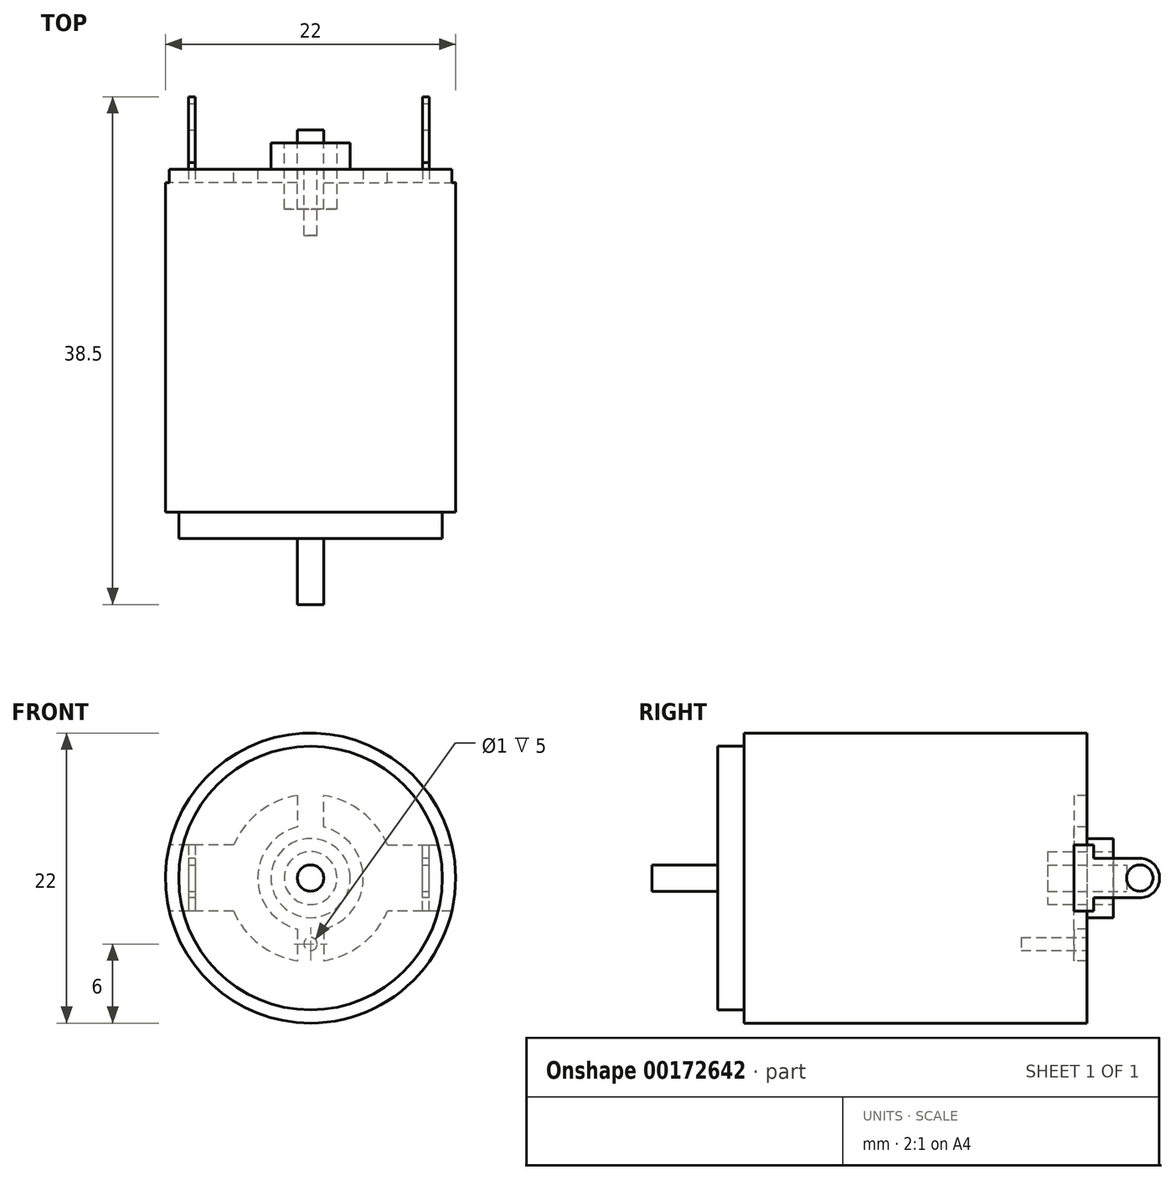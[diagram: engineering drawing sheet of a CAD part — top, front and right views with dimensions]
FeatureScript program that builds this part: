
annotation { "Feature Type Name" : "Feature", "Feature Type Description" : "" }
export const myFeature = defineFeature(function(context is Context, id is Id, definition is map)
    precondition{}
    {
        {
            var Q0;
            Q0=qCreatedBy(makeId("Front.planeOp"),FACE);
            var sketch = newSketch(context, id + "F0", { "sketchPlane" : qUnion([Q0])});
            skCircle(sketch, "E0", {"center": v(0, 0) * mm, "radius": 11 * mm});
            skSolve(sketch);
        }
        {
            var Q0;
            Q0 = qSketchRegion(id + "F0", true);
            extrude(context, id + "F1", {"entities" : qUnion([Q0]), "depth" : 26 * mm});
        }
        {
            var Q0;
            Q0=makeQuery(id+"F1.opExtrude","CAP_FACE",FACE,{"disambiguationData":[OSD([sQuery(id+"F0.wireOp",EDGE,"E0")])],"isStart":false});
            var sketch = newSketch(context, id + "F2", { "sketchPlane" : qUnion([Q0])});
            skCircle(sketch, "E1", {"center": v(0, 0) * mm, "radius": 10 * mm});
            skSolve(sketch);
        }
        {
            var Q0;
            Q0 = qSketchRegion(id + "F2", true);
            extrude(context, id + "F3", {"entities" : qUnion([Q0]), "operationType" : NewBodyOperationType.ADD, "depth" : 2 * mm});
        }
        {
            var Q0;
            Q0=makeQuery(id+"F3.opExtrude","CAP_FACE",FACE,{"disambiguationData":[OSD([sQuery(id+"F2.wireOp",EDGE,"E1")])],"isStart":false});
            var sketch = newSketch(context, id + "F4", { "sketchPlane" : qUnion([Q0])});
            skCircle(sketch, "E2", {"center": v(0, 0) * mm, "radius": 1 * mm});
            skSolve(sketch);
        }
        {
            var Q0;
            Q0 = qSketchRegion(id + "F4", true);
            extrude(context, id + "F5", {"entities" : qUnion([Q0]), "operationType" : NewBodyOperationType.ADD, "depth" : 5 * mm});
        }
        {
            var Q0;
            Q0=makeQuery(id+"F1.opExtrude","CAP_FACE",FACE,{"disambiguationData":[OSD([sQuery(id+"F0.wireOp",EDGE,"E0")])],"isStart":true});
            var sketch = newSketch(context, id + "F6", { "sketchPlane" : qUnion([Q0])});
            skArc(sketch, "E3", {"start": v(-5.84, -2.5) * mm, "mid": v(0, -6.35) * mm, "end": v(5.84, -2.5) * mm});
            skLineSegment(sketch, "E4", {"start": v(-5.84, 2.5) * mm, "end": v(-10.71, 2.5) * mm});
            skLineSegment(sketch, "E5", {"start": v(5.84, 2.5) * mm, "end": v(10.71, 2.5) * mm});
            skLineSegment(sketch, "E6", {"start": v(-10.71, -2.5) * mm, "end": v(-5.84, -2.5) * mm});
            skPoint(sketch, "E7", {"position": v(-5.84, 2.5) * mm});
            skPoint(sketch, "E8", {"position": v(-5.84, -2.5) * mm});
            skPoint(sketch, "E9", {"position": v(5.84, -2.5) * mm});
            skPoint(sketch, "E10", {"position": v(5.84, 2.5) * mm});
            skArc(sketch, "E11.trimOffspring", {"start": v(5.84, 2.5) * mm, "mid": v(0, 6.35) * mm, "end": v(-5.84, 2.5) * mm});
            skLineSegment(sketch, "E12.trimOffspring", {"start": v(5.84, -2.5) * mm, "end": v(10.71, -2.5) * mm});
            skSolve(sketch);
        }
        {
            var Q0;
            Q0=makeQuery(id+"F6.imprint","IMPRINT",FACE,{"disambiguationData":[TD([[makeQuery(id+"F6.imprint","IMPRINT",EDGE,{"derivedFrom":sQuery(id+"F6.wireOp",EDGE,"E3")}),1.0]])]});
            extrude(context, id + "F7", {"entities" : qUnion([Q0]), "operationType" : NewBodyOperationType.REMOVE, "oppositeDirection" : true, "depth" : 1 * mm});
        }
        {
            var Q0;
            Q0=makeQuery(id+"F7.boolean.opBoolean","COPY",FACE,{"derivedFrom":makeQuery(id+"F7.opExtrude","CAP_FACE",FACE,{"disambiguationData":[OSD([sQuery(id+"F0.wireOp",EDGE,"E0"),sQuery(id+"F6.wireOp",EDGE,"E3"),sQuery(id+"F6.wireOp",EDGE,"E4"),sQuery(id+"F6.wireOp",EDGE,"E5"),sQuery(id+"F6.wireOp",EDGE,"E6"),sQuery(id+"F6.wireOp",EDGE,"E11.trimOffspring"),sQuery(id+"F6.wireOp",EDGE,"E12.trimOffspring")])],"isStart":false})});
            var sketch = newSketch(context, id + "F8", { "sketchPlane" : qUnion([Q0])});
            skArc(sketch, "E13", {"start": v(-1, 3.87) * mm, "mid": v(-4, 0) * mm, "end": v(-1, -3.87) * mm});
            skLineSegment(sketch, "E14", {"start": v(-1, 3.87) * mm, "end": v(-1, 6.27) * mm});
            skLineSegment(sketch, "E15", {"start": v(-1, 6.27) * mm, "end": v(-1, 3.87) * mm});
            skLineSegment(sketch, "E16", {"start": v(1, 6.27) * mm, "end": v(1, 3.87) * mm});
            skArc(sketch, "E17.trimOffspring", {"start": v(1, -3.87) * mm, "mid": v(4, 0) * mm, "end": v(1, 3.87) * mm});
            skLineSegment(sketch, "E18.trimOffspring", {"start": v(-1, -3.87) * mm, "end": v(-1, -6.27) * mm});
            skLineSegment(sketch, "E19.trimOffspring", {"start": v(1, -3.87) * mm, "end": v(1, -6.27) * mm});
            skSolve(sketch);
        }
        {
            var Q0;
            Q0=makeQuery(id+"F8.imprint","IMPRINT",FACE,{"disambiguationData":[TD([[makeQuery(id+"F8.imprint","IMPRINT",EDGE,{"derivedFrom":sQuery(id+"F8.wireOp",EDGE,"E13")}),1.0]])]});
            extrude(context, id + "F9", {"entities" : qUnion([Q0]), "operationType" : NewBodyOperationType.ADD, "depth" : 1 * mm});
        }
        {
            var Q0;
            {var subQ0=sQuery(id+"F6.wireOp",EDGE,"E11.trimOffspring");var subQ1=sQuery(id+"F6.wireOp",EDGE,"E3");var subQ2=sQuery(id+"F0.wireOp",EDGE,"E0");var subQ4=makeQuery(id+"F1.opExtrude","CAP_FACE",FACE,{"disambiguationData":[OSD([subQ2])],"isStart":true});Q0=makeQuery(id+"F9.boolean.opBoolean","MERGE",FACE,{"derivedFrom":[makeQuery(id+"F7.boolean.opBoolean","SPLIT",FACE,{"disambiguationData":[TD([makeQuery(id+"F7.opExtrude","SWEPT_FACE",FACE,{"disambiguationData":[OSD([subQ1])]})])],"derivedFrom":subQ4}),makeQuery(id+"F7.boolean.opBoolean","SPLIT",FACE,{"disambiguationData":[TD([makeQuery(id+"F7.opExtrude","SWEPT_FACE",FACE,{"disambiguationData":[OSD([sQuery(id+"F6.wireOp",EDGE,"E4")])]})])],"derivedFrom":subQ4}),makeQuery(id+"F9.opExtrude","CAP_FACE",FACE,{"disambiguationData":[OSD([subQ1,subQ0,sQuery(id+"F8.wireOp",EDGE,"E13"),sQuery(id+"F8.wireOp",EDGE,"E15"),sQuery(id+"F8.wireOp",EDGE,"E16"),sQuery(id+"F8.wireOp",EDGE,"E17.trimOffspring"),sQuery(id+"F8.wireOp",EDGE,"E18.trimOffspring"),sQuery(id+"F8.wireOp",EDGE,"E19.trimOffspring")])],"isStart":false})]});}
            var sketch = newSketch(context, id + "F10", { "sketchPlane" : qUnion([Q0])});
            skCircle(sketch, "E20", {"center": v(0, 0) * mm, "radius": 3 * mm});
            skSolve(sketch);
        }
        {
            var Q0;
            Q0 = qSketchRegion(id + "F10", true);
            extrude(context, id + "F11", {"entities" : qUnion([Q0]), "operationType" : NewBodyOperationType.ADD, "depth" : 2 * mm});
        }
        {
            var Q0;
            Q0=makeQuery(id+"F11.opExtrude","CAP_FACE",FACE,{"disambiguationData":[OSD([sQuery(id+"F10.wireOp",EDGE,"E20")])],"isStart":false});
            var sketch = newSketch(context, id + "F12", { "sketchPlane" : qUnion([Q0])});
            skCircle(sketch, "E21", {"center": v(0, 0) * mm, "radius": 2 * mm});
            skCircle(sketch, "E22", {"center": v(0, 0) * mm, "radius": 1 * mm});
            skSolve(sketch);
        }
        {
            var Q0;
            Q0=makeQuery(id+"F12.imprint","IMPRINT",FACE,{"disambiguationData":[TD([[makeQuery(id+"F12.imprint","IMPRINT",EDGE,{"derivedFrom":sQuery(id+"F12.wireOp",EDGE,"E21")}),1.0]])]});
            extrude(context, id + "F13", {"entities" : qUnion([Q0]), "operationType" : NewBodyOperationType.REMOVE, "oppositeDirection" : true, "depth" : 5 * mm});
        }
        {
            var Q0;
            Q0=makeQuery(id+"F13.boolean.opBoolean","SPLIT",FACE,{"disambiguationData":[TD([makeQuery(id+"F13.opExtrude","SWEPT_FACE",FACE,{"disambiguationData":[OSD([sQuery(id+"F12.wireOp",EDGE,"E22")])]})])],"derivedFrom":makeQuery(id+"F11.opExtrude","CAP_FACE",FACE,{"disambiguationData":[OSD([sQuery(id+"F10.wireOp",EDGE,"E20")])],"isStart":false})});
            extrude(context, id + "F14", {"entities" : qUnion([Q0]), "operationType" : NewBodyOperationType.ADD, "depth" : 1 * mm});
        }
        {
            var Q0;
            {var subQ0=sQuery(id+"F6.wireOp",EDGE,"E11.trimOffspring");var subQ1=sQuery(id+"F6.wireOp",EDGE,"E3");var subQ2=sQuery(id+"F0.wireOp",EDGE,"E0");var subQ4=makeQuery(id+"F1.opExtrude","CAP_FACE",FACE,{"disambiguationData":[OSD([subQ2])],"isStart":true});Q0=makeQuery(id+"F9.boolean.opBoolean","MERGE",FACE,{"derivedFrom":[makeQuery(id+"F7.boolean.opBoolean","SPLIT",FACE,{"disambiguationData":[TD([makeQuery(id+"F7.opExtrude","SWEPT_FACE",FACE,{"disambiguationData":[OSD([subQ1])]})])],"derivedFrom":subQ4}),makeQuery(id+"F7.boolean.opBoolean","SPLIT",FACE,{"disambiguationData":[TD([makeQuery(id+"F7.opExtrude","SWEPT_FACE",FACE,{"disambiguationData":[OSD([sQuery(id+"F6.wireOp",EDGE,"E4")])]})])],"derivedFrom":subQ4}),makeQuery(id+"F9.opExtrude","CAP_FACE",FACE,{"disambiguationData":[OSD([subQ1,subQ0,sQuery(id+"F8.wireOp",EDGE,"E13"),sQuery(id+"F8.wireOp",EDGE,"E15"),sQuery(id+"F8.wireOp",EDGE,"E16"),sQuery(id+"F8.wireOp",EDGE,"E17.trimOffspring"),sQuery(id+"F8.wireOp",EDGE,"E18.trimOffspring"),sQuery(id+"F8.wireOp",EDGE,"E19.trimOffspring")])],"isStart":false})]});}
            var sketch = newSketch(context, id + "F15", { "sketchPlane" : qUnion([Q0])});
            skPoint(sketch, "E23", {"position": v(0, -5) * mm});
            skCircle(sketch, "E24", {"center": v(0, -5) * mm, "radius": 0.5 * mm});
            skSolve(sketch);
        }
        {
            var Q0;
            Q0=makeQuery(id+"F15.imprint","IMPRINT",FACE,{"disambiguationData":[TD([[makeQuery(id+"F15.imprint","IMPRINT",EDGE,{"derivedFrom":sQuery(id+"F15.wireOp",EDGE,"E24")}),1.0]])]});
            var Q1;
            Q1=sQuery(id+"F15.wireOp",EDGE,"E24");
            extrude(context, id + "F16", {"entities" : qUnion([Q0]), "operationType" : NewBodyOperationType.REMOVE, "surfaceEntities" : qUnion([Q1]), "oppositeDirection" : true, "depth" : 5 * mm});
        }
        {
            var Q0;
            {var subQ0=sQuery(id+"F6.wireOp",EDGE,"E6");var subQ1=sQuery(id+"F6.wireOp",EDGE,"E4");var subQ2=sQuery(id+"F6.wireOp",EDGE,"E3");var subQ3=sQuery(id+"F0.wireOp",EDGE,"E0");var subQ4=sQuery(id+"F6.wireOp",EDGE,"E11.trimOffspring");Q0=makeQuery(id+"F9.boolean.opBoolean","SPLIT",FACE,{"disambiguationData":[TD([makeQuery(id+"F7.boolean.opBoolean","COPY",FACE,{"derivedFrom":makeQuery(id+"F7.opExtrude","SWEPT_FACE",FACE,{"disambiguationData":[OSD([subQ1])]})})])],"derivedFrom":makeQuery(id+"F7.boolean.opBoolean","COPY",FACE,{"derivedFrom":makeQuery(id+"F7.opExtrude","CAP_FACE",FACE,{"disambiguationData":[OSD([subQ3,subQ2,subQ1,sQuery(id+"F6.wireOp",EDGE,"E5"),subQ0,subQ4,sQuery(id+"F6.wireOp",EDGE,"E12.trimOffspring")])],"isStart":false})})});}
            var sketch = newSketch(context, id + "F17", { "sketchPlane" : qUnion([Q0])});
            skPoint(sketch, "E25", {"position": v(-11, 0) * mm});
            skPoint(sketch, "E26", {"position": v(-9, 0) * mm});
            skLineSegment(sketch, "E27.bottom", {"start": v(-9, -2.5) * mm, "end": v(-8.5, -2.5) * mm});
            skLineSegment(sketch, "E27.top", {"start": v(-9, 2.5) * mm, "end": v(-8.5, 2.5) * mm});
            skLineSegment(sketch, "E27.left", {"start": v(-9, -2.5) * mm, "end": v(-9, 2.5) * mm});
            skLineSegment(sketch, "E27.right", {"start": v(-8.5, -2.5) * mm, "end": v(-8.5, 2.5) * mm});
            skSolve(sketch);
        }
        {
            var Q0;
            Q0 = qSketchRegion(id + "F17", true);
            extrude(context, id + "F18", {"entities" : qUnion([Q0]), "operationType" : NewBodyOperationType.ADD, "depth" : 1.5 * mm});
        }
        {
            var Q0;
            Q0=makeQuery(id+"F18.opExtrude","CAP_FACE",FACE,{"disambiguationData":[OSD([sQuery(id+"F17.wireOp",EDGE,"E27.bottom"),sQuery(id+"F17.wireOp",EDGE,"E27.top"),sQuery(id+"F17.wireOp",EDGE,"E27.left"),sQuery(id+"F17.wireOp",EDGE,"E27.right")])],"isStart":false});
            var sketch = newSketch(context, id + "F19", { "sketchPlane" : qUnion([Q0])});
            skPoint(sketch, "E28", {"position": v(-8.75, 0) * mm});
            skLineSegment(sketch, "E29.bottom", {"start": v(-9, 1.5) * mm, "end": v(-8.5, 1.5) * mm});
            skLineSegment(sketch, "E29.top", {"start": v(-9, -1.5) * mm, "end": v(-8.5, -1.5) * mm});
            skLineSegment(sketch, "E29.left", {"start": v(-9, 1.5) * mm, "end": v(-9, -1.5) * mm});
            skLineSegment(sketch, "E29.right", {"start": v(-8.5, 1.5) * mm, "end": v(-8.5, -1.5) * mm});
            skSolve(sketch);
        }
        {
            var Q0;
            Q0 = qSketchRegion(id + "F19", true);
            extrude(context, id + "F20", {"entities" : qUnion([Q0]), "operationType" : NewBodyOperationType.ADD, "depth" : 5 * mm});
        }
        {
            var Q0;
            {var subQ0=sQuery(id+"F6.wireOp",EDGE,"E11.trimOffspring");var subQ1=sQuery(id+"F6.wireOp",EDGE,"E5");var subQ2=sQuery(id+"F6.wireOp",EDGE,"E3");var subQ3=sQuery(id+"F0.wireOp",EDGE,"E0");var subQ4=sQuery(id+"F6.wireOp",EDGE,"E12.trimOffspring");Q0=makeQuery(id+"F9.boolean.opBoolean","SPLIT",FACE,{"disambiguationData":[TD([makeQuery(id+"F7.boolean.opBoolean","COPY",FACE,{"derivedFrom":makeQuery(id+"F7.opExtrude","SWEPT_FACE",FACE,{"disambiguationData":[OSD([subQ1])]})})])],"derivedFrom":makeQuery(id+"F7.boolean.opBoolean","COPY",FACE,{"derivedFrom":makeQuery(id+"F7.opExtrude","CAP_FACE",FACE,{"disambiguationData":[OSD([subQ3,subQ2,sQuery(id+"F6.wireOp",EDGE,"E4"),subQ1,sQuery(id+"F6.wireOp",EDGE,"E6"),subQ0,subQ4])],"isStart":false})})});}
            var sketch = newSketch(context, id + "F21", { "sketchPlane" : qUnion([Q0])});
            skPoint(sketch, "E30", {"position": v(11, 0) * mm});
            skPoint(sketch, "E31", {"position": v(9, 0) * mm});
            skLineSegment(sketch, "E32.bottom", {"start": v(8.75, 2.5) * mm, "end": v(9.25, 2.5) * mm});
            skLineSegment(sketch, "E32.top", {"start": v(8.75, -2.5) * mm, "end": v(9.25, -2.5) * mm});
            skLineSegment(sketch, "E32.left", {"start": v(8.75, 2.5) * mm, "end": v(8.75, -2.5) * mm});
            skLineSegment(sketch, "E32.right", {"start": v(9.25, 2.5) * mm, "end": v(9.25, -2.5) * mm});
            skSolve(sketch);
        }
        {
            var Q0;
            Q0=makeQuery(id+"F21.imprint","IMPRINT",FACE,{"disambiguationData":[TD([[makeQuery(id+"F21.imprint","IMPRINT",EDGE,{"derivedFrom":sQuery(id+"F21.wireOp",EDGE,"E32.bottom")}),-1.0]])]});
            extrude(context, id + "F22", {"entities" : qUnion([Q0]), "operationType" : NewBodyOperationType.ADD, "depth" : 1.5 * mm});
        }
        {
            var Q0;
            Q0=makeQuery(id+"F22.opExtrude","CAP_FACE",FACE,{"disambiguationData":[OSD([sQuery(id+"F21.wireOp",EDGE,"E32.bottom"),sQuery(id+"F21.wireOp",EDGE,"E32.top"),sQuery(id+"F21.wireOp",EDGE,"E32.left"),sQuery(id+"F21.wireOp",EDGE,"E32.right")])],"isStart":false});
            var sketch = newSketch(context, id + "F23", { "sketchPlane" : qUnion([Q0])});
            skPoint(sketch, "E33", {"position": v(9, 0) * mm});
            skLineSegment(sketch, "E34.bottom", {"start": v(8.75, 1.5) * mm, "end": v(9.25, 1.5) * mm});
            skLineSegment(sketch, "E34.top", {"start": v(8.75, -1.5) * mm, "end": v(9.25, -1.5) * mm});
            skLineSegment(sketch, "E34.left", {"start": v(8.75, 1.5) * mm, "end": v(8.75, -1.5) * mm});
            skLineSegment(sketch, "E34.right", {"start": v(9.25, 1.5) * mm, "end": v(9.25, -1.5) * mm});
            skSolve(sketch);
        }
        {
            var Q0;
            Q0 = qSketchRegion(id + "F23", true);
            extrude(context, id + "F24", {"entities" : qUnion([Q0]), "operationType" : NewBodyOperationType.ADD, "depth" : 5 * mm});
        }
        {
            var Q0;
            Q0=makeQuery(id+"F20.boolean.opBoolean","MERGE",FACE,{"derivedFrom":[makeQuery(id+"F18.opExtrude","SWEPT_FACE",FACE,{"disambiguationData":[OSD([sQuery(id+"F17.wireOp",EDGE,"E27.left")])]}),makeQuery(id+"F20.opExtrude","SWEPT_FACE",FACE,{"disambiguationData":[OSD([sQuery(id+"F19.wireOp",EDGE,"E29.left")])]})]});
            var sketch = newSketch(context, id + "F25", { "sketchPlane" : qUnion([Q0])});
            skPoint(sketch, "E35", {"position": v(4, 0) * mm});
            skArc(sketch, "E36", {"start": v(4, -1.5) * mm, "mid": v(5.5, 0) * mm, "end": v(4, 1.5) * mm});
            skPoint(sketch, "E37", {"position": v(4, 1.5) * mm});
            skPoint(sketch, "E38", {"position": v(4, -1.5) * mm});
            skCircle(sketch, "E39", {"center": v(4, 0) * mm, "radius": 1 * mm});
            skSolve(sketch);
        }
        {
            var Q0;
            {var subQ0=sQuery(id+"F25.wireOp",EDGE,"E36");var subQ1=sQuery(id+"F19.wireOp",EDGE,"E29.left");var subQ4=makeQuery(id+"F20.opExtrude","CAP_EDGE",EDGE,{"disambiguationData":[OSD([subQ1])],"isStart":false});var subQ5=makeQuery(id+"F25.imprint","INTERSECT",VERTEX,{"derivedFrom":[subQ4,subQ0]});Q0=makeQuery(id+"F25.imprint","IMPRINT",FACE,{"disambiguationData":[TD([[makeQuery(id+"F25.imprint","IMPRINT",EDGE,{"disambiguationData":[TD([[subQ5,-1.0]])],"derivedFrom":subQ0}),-1.0]])]});}
            extrude(context, id + "F26", {"entities" : qUnion([Q0]), "operationType" : NewBodyOperationType.REMOVE, "endBound" : BoundingType.THROUGH_ALL, "oppositeDirection" : true, "depth" : 25.4 * mm});
        }
        {
            var Q0;
            {var subQ0=sQuery(id+"F25.wireOp",EDGE,"E36");var subQ1=sQuery(id+"F19.wireOp",EDGE,"E29.left");var subQ4=makeQuery(id+"F20.opExtrude","CAP_EDGE",EDGE,{"disambiguationData":[OSD([subQ1])],"isStart":false});var subQ5=makeQuery(id+"F25.imprint","INTERSECT",VERTEX,{"derivedFrom":[subQ4,subQ0]});Q0=makeQuery(id+"F25.imprint","IMPRINT",FACE,{"disambiguationData":[TD([[makeQuery(id+"F25.imprint","IMPRINT",EDGE,{"disambiguationData":[TD([[subQ5,1.0]])],"derivedFrom":subQ0}),-1.0]])]});}
            extrude(context, id + "F27", {"entities" : qUnion([Q0]), "operationType" : NewBodyOperationType.REMOVE, "endBound" : BoundingType.THROUGH_ALL, "oppositeDirection" : true, "depth" : 25.4 * mm});
        }
        {
            var Q0;
            Q0=makeQuery(id+"F25.imprint","IMPRINT",FACE,{"disambiguationData":[TD([[makeQuery(id+"F25.imprint","IMPRINT",EDGE,{"derivedFrom":sQuery(id+"F25.wireOp",EDGE,"E39")}),1.0]])]});
            extrude(context, id + "F28", {"entities" : qUnion([Q0]), "operationType" : NewBodyOperationType.REMOVE, "endBound" : BoundingType.THROUGH_ALL, "oppositeDirection" : true, "depth" : 25.4 * mm});
        }
    });
